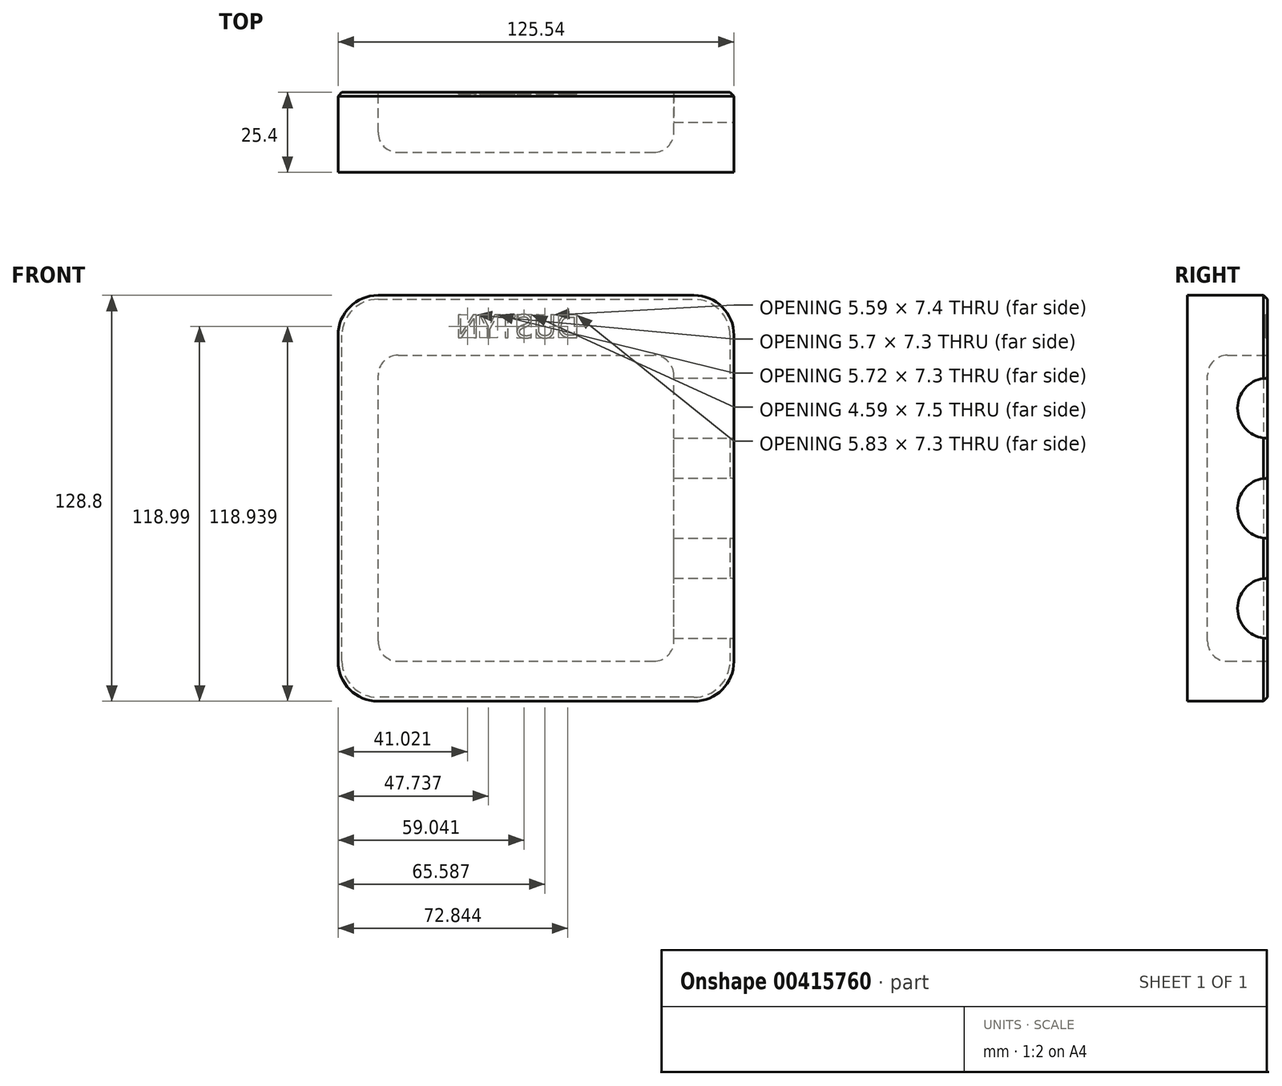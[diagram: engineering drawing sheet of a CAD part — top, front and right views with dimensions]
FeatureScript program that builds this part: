
annotation { "Feature Type Name" : "Feature", "Feature Type Description" : "" }
export const myFeature = defineFeature(function(context is Context, id is Id, definition is map)
    precondition{}
    {
        {
            var Q0;
            Q0=qCreatedBy(makeId("Front.planeOp"),FACE);
            var sketch = newSketch(context, id + "F0", { "sketchPlane" : qUnion([Q0])});
            skLineSegment(sketch, "E0.bottom", {"start": v(62.77, -64.4) * mm, "end": v(-62.77, -64.4) * mm});
            skLineSegment(sketch, "E0.top", {"start": v(62.77, 64.4) * mm, "end": v(-62.77, 64.4) * mm});
            skLineSegment(sketch, "E0.left", {"start": v(62.77, -64.4) * mm, "end": v(62.77, 64.4) * mm});
            skLineSegment(sketch, "E0.right", {"start": v(-62.77, -64.4) * mm, "end": v(-62.77, 64.4) * mm});
            skPoint(sketch, "E0.middle", {"position": v(0, 0) * mm});
            skSolve(sketch);
        }
        {
            var Q0;
            Q0=makeQuery(id+"F0.imprint","IMPRINT",FACE,{"disambiguationData":[TD([[makeQuery(id+"F0.imprint","IMPRINT",EDGE,{"derivedFrom":sQuery(id+"F0.wireOp",EDGE,"E0.bottom")}),-1.0]])]});
            extrude(context, id + "F1", {"entities" : qUnion([Q0]), "depth" : 25.4 * mm});
        }
        {
            var Q0;
            Q0=qCreatedBy(makeId("Front.planeOp"),FACE);
            var sketch = newSketch(context, id + "F2", { "sketchPlane" : qUnion([Q0])});
            skLineSegment(sketch, "E1.bottom", {"start": v(-50.07, -51.7) * mm, "end": v(43.72, -51.7) * mm});
            skLineSegment(sketch, "E1.top", {"start": v(-50.07, 45.35) * mm, "end": v(43.72, 45.35) * mm});
            skLineSegment(sketch, "E1.left", {"start": v(-50.07, -51.7) * mm, "end": v(-50.07, 45.35) * mm});
            skLineSegment(sketch, "E1.right", {"start": v(43.72, -51.7) * mm, "end": v(43.72, 45.35) * mm});
            skSolve(sketch);
        }
        {
            var Q0;
            Q0 = qSketchRegion(id + "F2", true);
            extrude(context, id + "F3", {"entities" : qUnion([Q0]), "operationType" : NewBodyOperationType.REMOVE, "depth" : 19.05 * mm});
        }
        {
            var Q0;
            Q0=makeQuery(id+"F1.opExtrude","SWEPT_EDGE",EDGE,{"disambiguationData":[OSD([sQuery(id+"F0.wireOp",EDGE,"E0.top"),sQuery(id+"F0.wireOp",EDGE,"E0.right")])]});
            var Q1;
            Q1=makeQuery(id+"F1.opExtrude","SWEPT_EDGE",EDGE,{"disambiguationData":[OSD([sQuery(id+"F0.wireOp",EDGE,"E0.top"),sQuery(id+"F0.wireOp",EDGE,"E0.left")])]});
            var Q2;
            Q2=makeQuery(id+"F1.opExtrude","SWEPT_EDGE",EDGE,{"disambiguationData":[OSD([sQuery(id+"F0.wireOp",EDGE,"E0.bottom"),sQuery(id+"F0.wireOp",EDGE,"E0.right")])]});
            var Q3;
            Q3=makeQuery(id+"F1.opExtrude","SWEPT_EDGE",EDGE,{"disambiguationData":[OSD([sQuery(id+"F0.wireOp",EDGE,"E0.bottom"),sQuery(id+"F0.wireOp",EDGE,"E0.left")])]});
            fillet(context, id + "F4", {"entities" : qUnion([Q0, Q1, Q2, Q3]), "radius" : 12.7 * mm, "tangentPropagation" : true, "allowEdgeOverflow" : false});
        }
        {
            var Q0;
            Q0=makeQuery(id+"F3.boolean.opBoolean","COPY",EDGE,{"derivedFrom":makeQuery(id+"F3.opExtrude","SWEPT_EDGE",EDGE,{"disambiguationData":[OSD([sQuery(id+"F2.wireOp",EDGE,"E1.bottom"),sQuery(id+"F2.wireOp",EDGE,"E1.left")])]})});
            var Q1;
            Q1=makeQuery(id+"F3.boolean.opBoolean","COPY",EDGE,{"derivedFrom":makeQuery(id+"F3.opExtrude","SWEPT_EDGE",EDGE,{"disambiguationData":[OSD([sQuery(id+"F2.wireOp",EDGE,"E1.top"),sQuery(id+"F2.wireOp",EDGE,"E1.left")])]})});
            var Q2;
            Q2=makeQuery(id+"F3.boolean.opBoolean","COPY",EDGE,{"derivedFrom":makeQuery(id+"F3.opExtrude","SWEPT_EDGE",EDGE,{"disambiguationData":[OSD([sQuery(id+"F2.wireOp",EDGE,"E1.top"),sQuery(id+"F2.wireOp",EDGE,"E1.right")])]})});
            var Q3;
            Q3=makeQuery(id+"F3.boolean.opBoolean","COPY",EDGE,{"derivedFrom":makeQuery(id+"F3.opExtrude","SWEPT_EDGE",EDGE,{"disambiguationData":[OSD([sQuery(id+"F2.wireOp",EDGE,"E1.bottom"),sQuery(id+"F2.wireOp",EDGE,"E1.right")])]})});
            fillet(context, id + "F5", {"entities" : qUnion([Q0, Q1, Q2, Q3]), "radius" : 6.35 * mm, "tangentPropagation" : true, "allowEdgeOverflow" : false});
        }
        {
            var Q0;
            Q0=makeQuery(id+"F1.opExtrude","CAP_EDGE",EDGE,{"disambiguationData":[OSD([sQuery(id+"F0.wireOp",EDGE,"E0.right")])],"isStart":true});
            var Q1;
            Q1=makeQuery(id+"F3.boolean.opBoolean","COPY",EDGE,{"derivedFrom":makeQuery(id+"F3.opExtrude","CAP_EDGE",EDGE,{"disambiguationData":[OSD([sQuery(id+"F2.wireOp",EDGE,"E1.left")])],"isStart":true})});
            chamfer(context, id + "F6", {"entities" : qUnion([Q0, Q1]), "width" : 1.27 * mm, "tangentPropagation" : true});
        }
        {
            var Q0;
            Q0=makeQuery(id+"F3.boolean.opBoolean","COPY",EDGE,{"derivedFrom":makeQuery(id+"F3.opExtrude","CAP_EDGE",EDGE,{"disambiguationData":[OSD([sQuery(id+"F2.wireOp",EDGE,"E1.top")])],"isStart":false})});
            fillet(context, id + "F7", {"entities" : qUnion([Q0]), "radius" : 6.35 * mm, "tangentPropagation" : true, "allowEdgeOverflow" : false});
        }
        {
            var Q0;
            Q0=makeQuery(id+"F1.opExtrude","CAP_FACE",FACE,{"disambiguationData":[OSD([sQuery(id+"F0.wireOp",EDGE,"E0.bottom"),sQuery(id+"F0.wireOp",EDGE,"E0.top"),sQuery(id+"F0.wireOp",EDGE,"E0.left"),sQuery(id+"F0.wireOp",EDGE,"E0.right")])],"isStart":true});
            var sketch = newSketch(context, id + "F8", { "sketchPlane" : qUnion([Q0])});
            skText(sketch, "E2", { "text": "DUSTYN", "fontName": "OpenSans-Regular.ttf"});
            const initialGuessF8  = {"E2": [-0.01399, 0.05094, 1, 0, 0.00736]};
            skSetInitialGuess(sketch, initialGuessF8);
            skSolve(sketch);
        }
        {
            var Q0;
            Q0=makeQuery(id+"F8.imprint","IMPRINT",FACE,{"disambiguationData":[TD([[makeQuery(id+"F8.imprint","IMPRINT",EDGE,{"derivedFrom":sQuery(id+"F8.wireOp",EDGE,"E2.sketch_text.stroke-0")}),-1.0]])]});
            var Q1;
            Q1=makeQuery(id+"F8.imprint","IMPRINT",FACE,{"disambiguationData":[TD([[makeQuery(id+"F8.imprint","IMPRINT",EDGE,{"derivedFrom":sQuery(id+"F8.wireOp",EDGE,"E2.sketch_text.stroke-14")}),-1.0]])]});
            var Q2;
            Q2=makeQuery(id+"F8.imprint","IMPRINT",FACE,{"disambiguationData":[TD([[makeQuery(id+"F8.imprint","IMPRINT",EDGE,{"derivedFrom":sQuery(id+"F8.wireOp",EDGE,"E2.sketch_text.stroke-28")}),-1.0]])]});
            var Q3;
            Q3=makeQuery(id+"F8.imprint","IMPRINT",FACE,{"disambiguationData":[TD([[makeQuery(id+"F8.imprint","IMPRINT",EDGE,{"derivedFrom":sQuery(id+"F8.wireOp",EDGE,"E2.sketch_text.stroke-53")}),-1.0]])]});
            var Q4;
            Q4=makeQuery(id+"F8.imprint","IMPRINT",FACE,{"disambiguationData":[TD([[makeQuery(id+"F8.imprint","IMPRINT",EDGE,{"derivedFrom":sQuery(id+"F8.wireOp",EDGE,"E2.sketch_text.stroke-61")}),-1.0]])]});
            var Q5;
            Q5=makeQuery(id+"F8.imprint","IMPRINT",FACE,{"disambiguationData":[TD([[makeQuery(id+"F8.imprint","IMPRINT",EDGE,{"derivedFrom":sQuery(id+"F8.wireOp",EDGE,"E2.sketch_text.stroke-70")}),-1.0]])]});
            extrude(context, id + "F9", {"entities" : qUnion([Q0, Q1, Q2, Q3, Q4, Q5]), "operationType" : NewBodyOperationType.REMOVE, "oppositeDirection" : true, "depth" : 0.5 * mm});
        }
        {
            var Q0;
            Q0=makeQuery(id+"F1.opExtrude","SWEPT_FACE",FACE,{"disambiguationData":[OSD([sQuery(id+"F0.wireOp",EDGE,"E0.left")])]});
            var sketch = newSketch(context, id + "F10", { "sketchPlane" : qUnion([Q0])});
            skCircle(sketch, "E3", {"center": v(0, 28.57) * mm, "radius": 9.53 * mm});
            skCircle(sketch, "E4", {"center": v(0, -3.18) * mm, "radius": 9.53 * mm});
            skCircle(sketch, "E5", {"center": v(0, -34.93) * mm, "radius": 9.53 * mm});
            skSolve(sketch);
        }
        {
            var Q0;
            {var subQ0=sQuery(id+"F10.wireOp",EDGE,"E3");var subQ1=sQuery(id+"F0.wireOp",EDGE,"E0.left");var subQ2=makeQuery(id+"F6.opChamfer","BLEND_EDGE",EDGE,{"blendedFrom":[makeQuery(id+"F1.opExtrude","CAP_EDGE",EDGE,{"disambiguationData":[OSD([subQ1])],"isStart":true}),makeQuery(id+"F1.opExtrude","SWEPT_FACE",FACE,{"disambiguationData":[OSD([subQ1])]})],"blendedInto":[makeQuery(id+"F1.opExtrude","SWEPT_FACE",FACE,{"disambiguationData":[OSD([subQ1])]})]});var subQ3=makeQuery(id+"F10.imprint","INTERSECT",VERTEX,{"disambiguationData":[OD(0.0)],"derivedFrom":[subQ2,subQ0]});Q0=makeQuery(id+"F10.imprint","IMPRINT",FACE,{"disambiguationData":[TD([[makeQuery(id+"F10.imprint","IMPRINT",EDGE,{"disambiguationData":[TD([[subQ3,-1.0]])],"derivedFrom":subQ0}),1.0]])]});}
            var Q1;
            {var subQ0=sQuery(id+"F10.wireOp",EDGE,"E3");var subQ1=sQuery(id+"F0.wireOp",EDGE,"E0.left");var subQ2=makeQuery(id+"F6.opChamfer","BLEND_EDGE",EDGE,{"blendedFrom":[makeQuery(id+"F1.opExtrude","CAP_EDGE",EDGE,{"disambiguationData":[OSD([subQ1])],"isStart":true}),makeQuery(id+"F1.opExtrude","SWEPT_FACE",FACE,{"disambiguationData":[OSD([subQ1])]})],"blendedInto":[makeQuery(id+"F1.opExtrude","SWEPT_FACE",FACE,{"disambiguationData":[OSD([subQ1])]})]});var subQ3=makeQuery(id+"F10.imprint","INTERSECT",VERTEX,{"disambiguationData":[OD(0.0)],"derivedFrom":[subQ2,subQ0]});Q1=makeQuery(id+"F10.imprint","IMPRINT",FACE,{"disambiguationData":[TD([[makeQuery(id+"F10.imprint","IMPRINT",EDGE,{"disambiguationData":[TD([[subQ3,1.0]])],"derivedFrom":subQ0}),1.0]])]});}
            var Q2;
            {var subQ0=sQuery(id+"F10.wireOp",EDGE,"E4");var subQ1=sQuery(id+"F0.wireOp",EDGE,"E0.left");var subQ2=makeQuery(id+"F6.opChamfer","BLEND_EDGE",EDGE,{"blendedFrom":[makeQuery(id+"F1.opExtrude","CAP_EDGE",EDGE,{"disambiguationData":[OSD([subQ1])],"isStart":true}),makeQuery(id+"F1.opExtrude","SWEPT_FACE",FACE,{"disambiguationData":[OSD([subQ1])]})],"blendedInto":[makeQuery(id+"F1.opExtrude","SWEPT_FACE",FACE,{"disambiguationData":[OSD([subQ1])]})]});var subQ3=makeQuery(id+"F10.imprint","INTERSECT",VERTEX,{"disambiguationData":[OD(0.0)],"derivedFrom":[subQ2,subQ0]});Q2=makeQuery(id+"F10.imprint","IMPRINT",FACE,{"disambiguationData":[TD([[makeQuery(id+"F10.imprint","IMPRINT",EDGE,{"disambiguationData":[TD([[subQ3,1.0]])],"derivedFrom":subQ0}),1.0]])]});}
            var Q3;
            {var subQ0=sQuery(id+"F10.wireOp",EDGE,"E4");var subQ1=sQuery(id+"F0.wireOp",EDGE,"E0.left");var subQ2=makeQuery(id+"F6.opChamfer","BLEND_EDGE",EDGE,{"blendedFrom":[makeQuery(id+"F1.opExtrude","CAP_EDGE",EDGE,{"disambiguationData":[OSD([subQ1])],"isStart":true}),makeQuery(id+"F1.opExtrude","SWEPT_FACE",FACE,{"disambiguationData":[OSD([subQ1])]})],"blendedInto":[makeQuery(id+"F1.opExtrude","SWEPT_FACE",FACE,{"disambiguationData":[OSD([subQ1])]})]});var subQ3=makeQuery(id+"F10.imprint","INTERSECT",VERTEX,{"disambiguationData":[OD(0.0)],"derivedFrom":[subQ2,subQ0]});Q3=makeQuery(id+"F10.imprint","IMPRINT",FACE,{"disambiguationData":[TD([[makeQuery(id+"F10.imprint","IMPRINT",EDGE,{"disambiguationData":[TD([[subQ3,-1.0]])],"derivedFrom":subQ0}),1.0]])]});}
            var Q4;
            {var subQ0=sQuery(id+"F10.wireOp",EDGE,"E5");var subQ1=sQuery(id+"F0.wireOp",EDGE,"E0.left");var subQ2=makeQuery(id+"F6.opChamfer","BLEND_EDGE",EDGE,{"blendedFrom":[makeQuery(id+"F1.opExtrude","CAP_EDGE",EDGE,{"disambiguationData":[OSD([subQ1])],"isStart":true}),makeQuery(id+"F1.opExtrude","SWEPT_FACE",FACE,{"disambiguationData":[OSD([subQ1])]})],"blendedInto":[makeQuery(id+"F1.opExtrude","SWEPT_FACE",FACE,{"disambiguationData":[OSD([subQ1])]})]});var subQ3=makeQuery(id+"F10.imprint","INTERSECT",VERTEX,{"disambiguationData":[OD(0.0)],"derivedFrom":[subQ2,subQ0]});Q4=makeQuery(id+"F10.imprint","IMPRINT",FACE,{"disambiguationData":[TD([[makeQuery(id+"F10.imprint","IMPRINT",EDGE,{"disambiguationData":[TD([[subQ3,-1.0]])],"derivedFrom":subQ0}),1.0]])]});}
            var Q5;
            {var subQ0=sQuery(id+"F10.wireOp",EDGE,"E5");var subQ1=sQuery(id+"F0.wireOp",EDGE,"E0.left");var subQ2=makeQuery(id+"F6.opChamfer","BLEND_EDGE",EDGE,{"blendedFrom":[makeQuery(id+"F1.opExtrude","CAP_EDGE",EDGE,{"disambiguationData":[OSD([subQ1])],"isStart":true}),makeQuery(id+"F1.opExtrude","SWEPT_FACE",FACE,{"disambiguationData":[OSD([subQ1])]})],"blendedInto":[makeQuery(id+"F1.opExtrude","SWEPT_FACE",FACE,{"disambiguationData":[OSD([subQ1])]})]});var subQ3=makeQuery(id+"F10.imprint","INTERSECT",VERTEX,{"disambiguationData":[OD(0.0)],"derivedFrom":[subQ2,subQ0]});Q5=makeQuery(id+"F10.imprint","IMPRINT",FACE,{"disambiguationData":[TD([[makeQuery(id+"F10.imprint","IMPRINT",EDGE,{"disambiguationData":[TD([[subQ3,1.0]])],"derivedFrom":subQ0}),1.0]])]});}
            extrude(context, id + "F11", {"entities" : qUnion([Q0, Q1, Q2, Q3, Q4, Q5]), "operationType" : NewBodyOperationType.REMOVE, "endBound" : BoundingType.UP_TO_NEXT, "oppositeDirection" : true, "depth" : 25.4 * mm});
        }
    });
